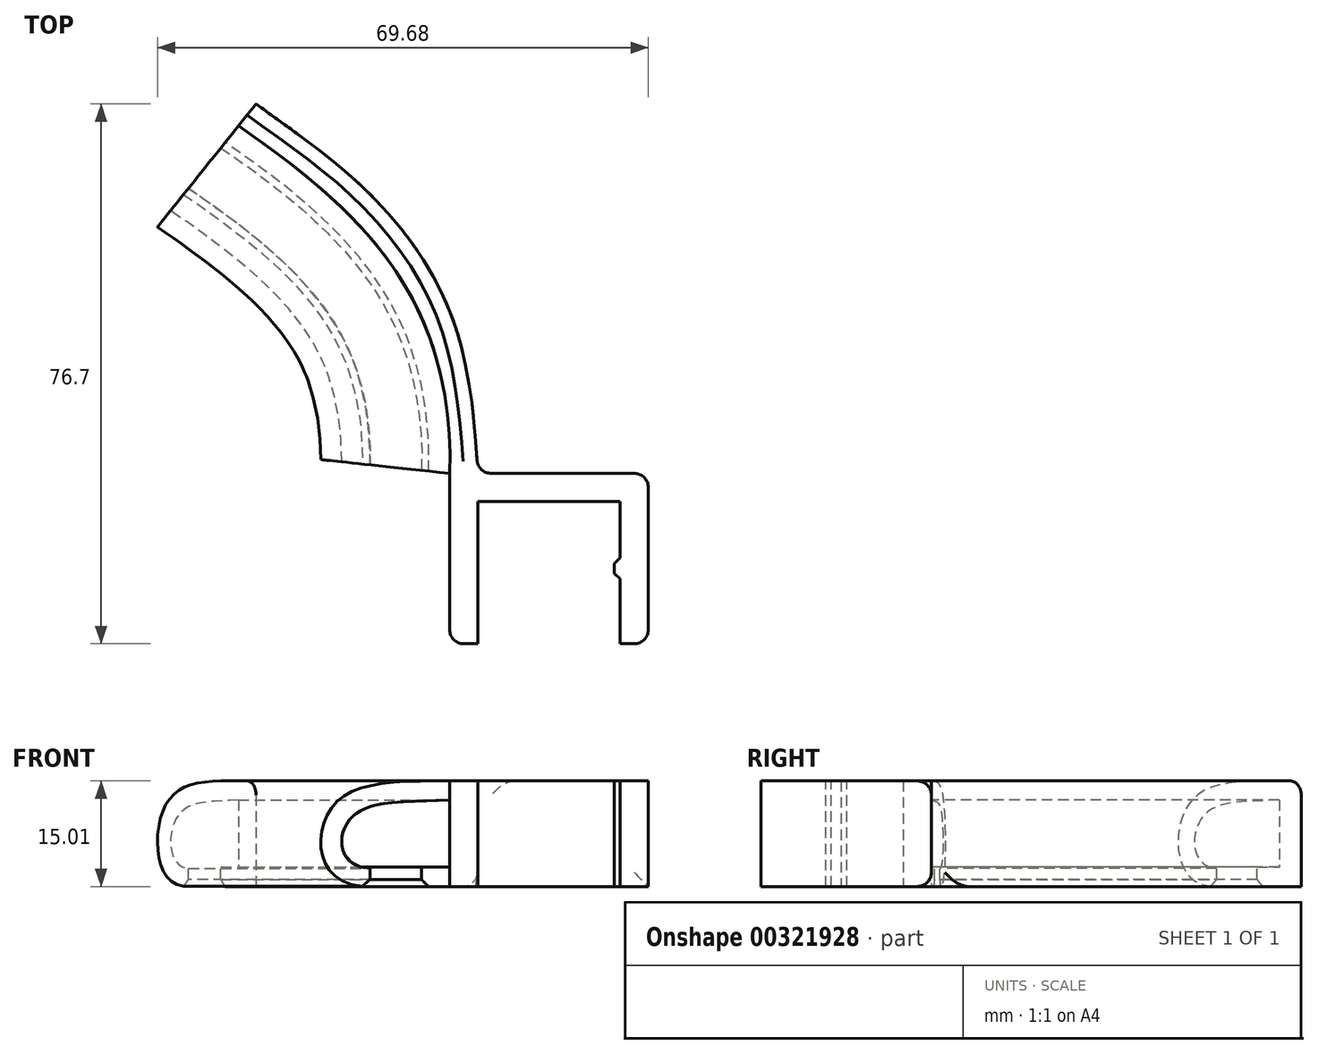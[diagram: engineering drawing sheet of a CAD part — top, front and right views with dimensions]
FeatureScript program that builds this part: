
annotation { "Feature Type Name" : "Feature", "Feature Type Description" : "" }
export const myFeature = defineFeature(function(context is Context, id is Id, definition is map)
    precondition{}
    {
        {
            var Q0;
            Q0=qCreatedBy(makeId("Top.planeOp"),FACE);
            var sketch = newSketch(context, id + "F0", { "sketchPlane" : qUnion([Q0])});
            skLineSegment(sketch, "E0.bottom", {"start": v(-53, -25.93) * mm, "end": v(-24.8, -25.93) * mm});
            skLineSegment(sketch, "E0.top", {"start": v(-53, -50.13) * mm, "end": v(-49, -50.13) * mm});
            skLineSegment(sketch, "E0.left", {"start": v(-53, -25.93) * mm, "end": v(-53, -50.13) * mm});
            skLineSegment(sketch, "E0.right", {"start": v(-24.8, -25.93) * mm, "end": v(-24.8, -50.13) * mm});
            skLineSegment(sketch, "E1", {"start": v(-49, -50.13) * mm, "end": v(-49, -29.93) * mm});
            skLineSegment(sketch, "E2", {"start": v(-49, -29.93) * mm, "end": v(-28.8, -29.93) * mm});
            skLineSegment(sketch, "E3", {"start": v(-28.8, -29.93) * mm, "end": v(-28.8, -50.13) * mm});
            skLineSegment(sketch, "E4.trimOffspring", {"start": v(-28.8, -50.13) * mm, "end": v(-24.8, -50.13) * mm});
            skFitSpline(sketch, "E5", {"points": [v(-53, -25.93) * mm, v(-56.82, -4.17) * mm, v(-68.68, 12.18) * mm, v(-83, 23.45) * mm], "startDerivative": vector(2.46, 64.33) * mm, "endDerivative": vector(-42.16, 29.22) * mm});
            skFitSpline(sketch, "E6", {"points": [v(-49, -25.93) * mm, v(-53, -2.83) * mm, v(-66.01, 15.37) * mm, v(-80.5, 26.57) * mm], "startDerivative": vector(-3.69, 66.34) * mm, "endDerivative": vector(-42.7, 31.6) * mm});
            skLineSegment(sketch, "E7", {"start": v(-83, 23.45) * mm, "end": v(-80.5, 26.57) * mm});
            skSolve(sketch);
        }
        {
            var Q0;
            Q0=makeQuery(id+"F0.imprint","IMPRINT",FACE,{"disambiguationData":[TD([[makeQuery(id+"F0.imprint","IMPRINT",EDGE,{"derivedFrom":sQuery(id+"F0.wireOp",EDGE,"E0.top")}),1.0]])]});
            var Q1;
            {var subQ2=sQuery(id+"F0.wireOp",EDGE,"E5");Q1=makeQuery(id+"F0.imprint","IMPRINT",FACE,{"disambiguationData":[TD([[makeQuery(id+"F0.imprint","IMPRINT",EDGE,{"derivedFrom":subQ2}),-1.0]])]});}
            extrude(context, id + "F1", {"entities" : qUnion([Q0, Q1]), "depth" : 15 * mm, "offsetDistance" : 25 * mm});
        }
        {
            var Q0;
            Q0=makeQuery(id+"F1.opExtrude","SWEPT_FACE",FACE,{"disambiguationData":[OSD([sQuery(id+"F0.wireOp",EDGE,"E7")])]});
            var sketch = newSketch(context, id + "F2", { "sketchPlane" : qUnion([Q0])});
            skLineSegment(sketch, "E8", {"start": v(33.54, 0) * mm, "end": v(37.54, 0) * mm});
            skLineSegment(sketch, "E9", {"start": v(37.54, 0) * mm, "end": v(37.54, 2.8) * mm});
            skLineSegment(sketch, "E10", {"start": v(37.54, 2.8) * mm, "end": v(33.54, 2.8) * mm});
            skFitSpline(sketch, "E11", {"points": [v(33.54, 15) * mm, v(49.36, 12.31) * mm, v(51.8, 4.84) * mm, v(44.94, 0) * mm], "startDerivative": vector(51.93, 0.4) * mm, "endDerivative": vector(-44.36, 0) * mm});
            skFitSpline(sketch, "E12", {"points": [v(33.54, 12.27) * mm, v(46.66, 10.53) * mm, v(48.95, 6.62) * mm, v(44.88, 2.55) * mm], "startDerivative": vector(47.89, -1.17) * mm, "endDerivative": vector(-33.03, -2.1) * mm});
            skLineSegment(sketch, "E13", {"start": v(44.94, 0) * mm, "end": v(44.88, 2.55) * mm});
            skSolve(sketch);
        }
        {
            var Q0;
            {var subQ0=sQuery(id+"F2.wireOp",EDGE,"E11");Q0=makeQuery(id+"F2.imprint","IMPRINT",FACE,{"disambiguationData":[TD([[makeQuery(id+"F2.imprint","IMPRINT",EDGE,{"derivedFrom":subQ0}),-1.0]])]});}
            var Q1;
            {var subQ0=sQuery(id+"F2.wireOp",EDGE,"E8");Q1=makeQuery(id+"F2.imprint","IMPRINT",FACE,{"disambiguationData":[TD([[makeQuery(id+"F2.imprint","IMPRINT",EDGE,{"derivedFrom":subQ0}),1.0]])]});}
            var Q2;
            Q2=makeQuery(id+"F1.opExtrude","CAP_EDGE",EDGE,{"disambiguationData":[OSD([sQuery(id+"F0.wireOp",EDGE,"E5")])],"isStart":true});
            sweep(context, id + "F3", {"operationType" : NewBodyOperationType.ADD, "profiles" : qUnion([Q0, Q1]), "path" : qUnion([Q2])});
        }
        {
            var Q0;
            Q0=makeQuery(id+"F3.opSweep","SWEPT_EDGE",EDGE,{"disambiguationData":[OSD([sQuery(id+"F0.wireOp",EDGE,"E5"),sQuery(id+"F2.wireOp",EDGE,"E11"),sQuery(id+"F2.wireOp",EDGE,"E13")])]});
            var Q1;
            Q1=makeQuery(id+"F3.opSweep","SWEPT_EDGE",EDGE,{"disambiguationData":[OSD([sQuery(id+"F0.wireOp",EDGE,"E5"),sQuery(id+"F2.wireOp",EDGE,"E8"),sQuery(id+"F2.wireOp",EDGE,"E9")])]});
            chamfer(context, id + "F4", {"entities" : qUnion([Q0, Q1]), "width" : 1 * mm, "tangentPropagation" : true});
        }
        {
            var Q0;
            Q0=makeQuery(id+"F1.opExtrude","CAP_EDGE",EDGE,{"disambiguationData":[OSD([sQuery(id+"F0.wireOp",EDGE,"E6")])],"isStart":false});
            var Q1;
            Q1=makeQuery(id+"F3.opSweep","SWEPT_EDGE",EDGE,{"disambiguationData":[OSD([sQuery(id+"F0.wireOp",EDGE,"E5"),sQuery(id+"F0.wireOp",EDGE,"E7"),sQuery(id+"F2.wireOp",EDGE,"E12")])]});
            var Q2;
            Q2=makeQuery(id+"F1.opExtrude","SWEPT_EDGE",EDGE,{"disambiguationData":[OSD([sQuery(id+"F0.wireOp",EDGE,"E0.bottom"),sQuery(id+"F0.wireOp",EDGE,"E0.right")])]});
            var Q3;
            Q3=makeQuery(id+"F1.opExtrude","SWEPT_EDGE",EDGE,{"disambiguationData":[OSD([sQuery(id+"F0.wireOp",EDGE,"E0.top"),sQuery(id+"F0.wireOp",EDGE,"E0.left")])]});
            var Q4;
            Q4=makeQuery(id+"F1.opExtrude","SWEPT_EDGE",EDGE,{"disambiguationData":[OSD([sQuery(id+"F0.wireOp",EDGE,"E0.right"),sQuery(id+"F0.wireOp",EDGE,"E4.trimOffspring")])]});
            var Q5;
            Q5=makeQuery(id+"F1.opExtrude","SWEPT_EDGE",EDGE,{"disambiguationData":[OSD([sQuery(id+"F0.wireOp",EDGE,"E0.bottom"),sQuery(id+"F0.wireOp",EDGE,"E6")])]});
            var Q6;
            Q6=makeQuery(id+"F1.opExtrude","CAP_EDGE",EDGE,{"disambiguationData":[OSD([sQuery(id+"F0.wireOp",EDGE,"E0.bottom")])],"isStart":true});
            fillet(context, id + "F5", {"entities" : qUnion([Q0, Q1, Q2, Q3, Q4, Q5, Q6]), "tangentPropagation" : true, "radius" : 2 * mm, "defaultsChanged" : false, "vertexSettings" : [], "allowEdgeOverflow" : false});
        }
        {
            var Q0;
            Q0=makeQuery(id+"F1.opExtrude","SWEPT_FACE",FACE,{"disambiguationData":[OSD([sQuery(id+"F0.wireOp",EDGE,"E3")])]});
            var sketch = newSketch(context, id + "F6", { "sketchPlane" : qUnion([Q0])});
            skLineSegment(sketch, "E14", {"start": v(37.93, 0) * mm, "end": v(37.93, 15) * mm});
            skLineSegment(sketch, "E15", {"start": v(40.93, 0) * mm, "end": v(40.93, 15) * mm});
            skSolve(sketch);
        }
        {
            var Q0;
            {var subQ0=sQuery(id+"F6.wireOp",EDGE,"E14");Q0=makeQuery(id+"F6.imprint","IMPRINT",FACE,{"disambiguationData":[TD([[makeQuery(id+"F6.imprint","IMPRINT",EDGE,{"derivedFrom":subQ0}),-1.0]])]});}
            extrude(context, id + "F7", {"entities" : qUnion([Q0]), "operationType" : NewBodyOperationType.ADD, "depth" : 0.8 * mm, "offsetDistance" : 25 * mm});
        }
        {
            var Q0;
            Q0=makeQuery(id+"F7.opExtrude","CAP_EDGE",EDGE,{"disambiguationData":[OSD([sQuery(id+"F6.wireOp",EDGE,"E15")])],"isStart":false});
            var Q1;
            Q1=makeQuery(id+"F7.opExtrude","CAP_EDGE",EDGE,{"disambiguationData":[OSD([sQuery(id+"F6.wireOp",EDGE,"E14")])],"isStart":false});
            chamfer(context, id + "F8", {"entities" : qUnion([Q0, Q1]), "width" : 0.8 * mm, "tangentPropagation" : true});
        }
    });
